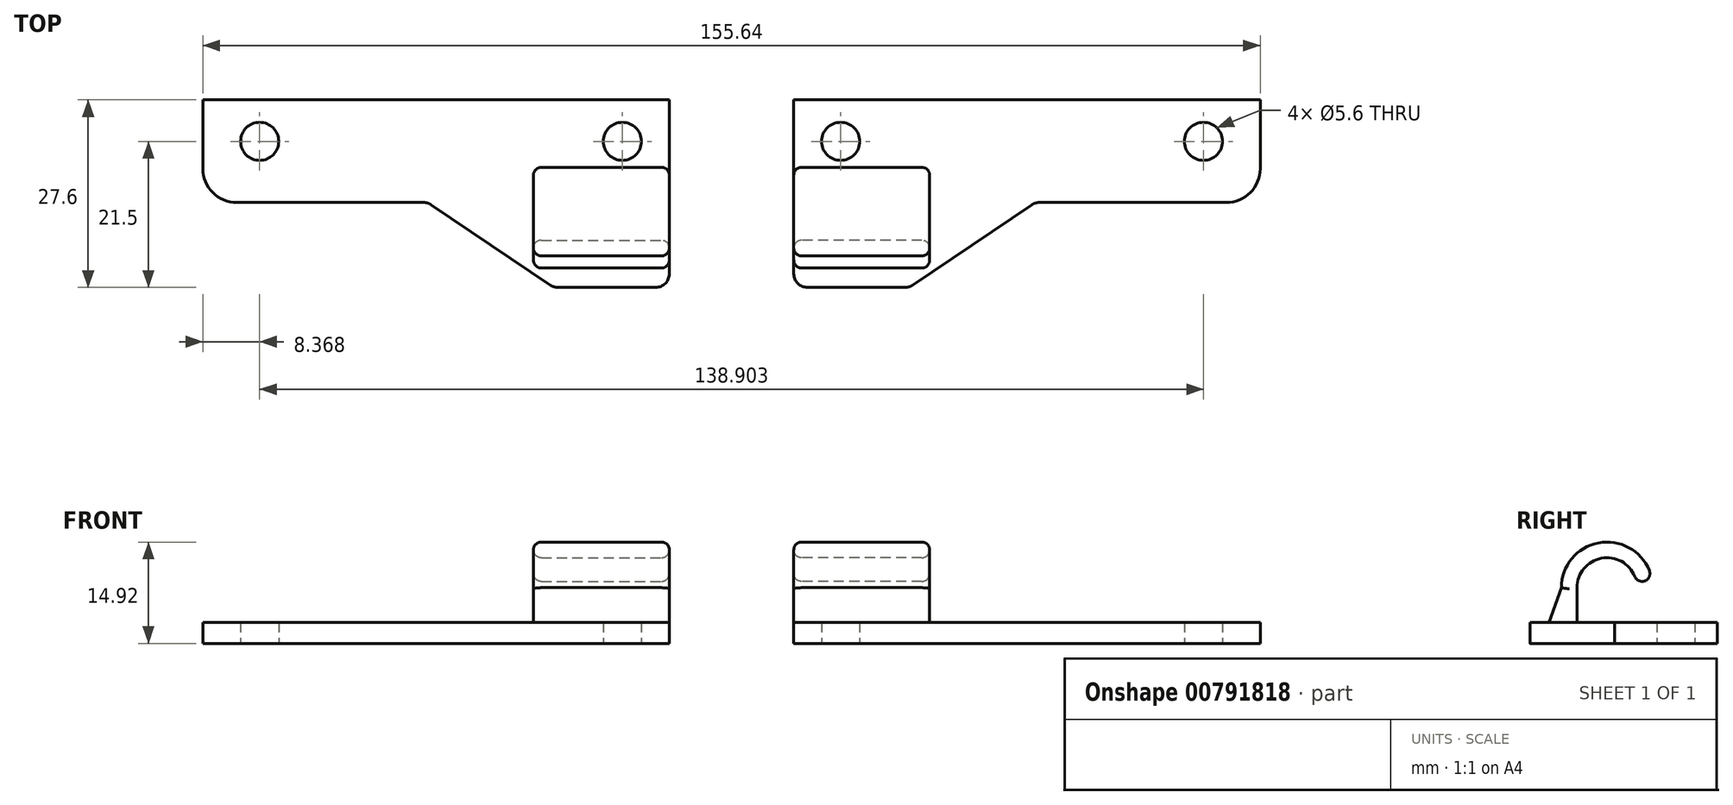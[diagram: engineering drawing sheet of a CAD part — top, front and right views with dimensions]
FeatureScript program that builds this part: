
annotation { "Feature Type Name" : "Feature", "Feature Type Description" : "" }
export const myFeature = defineFeature(function(context is Context, id is Id, definition is map)
    precondition{}
    {
        {
            var Q0;
            Q0=qCreatedBy(makeId("Top.planeOp"),FACE);
            var sketch = newSketch(context, id + "F0", { "sketchPlane" : qUnion([Q0])});
            skCircle(sketch, "E0", {"center": v(-17.35, 21.4) * mm, "radius": 2.8 * mm});
            skLineSegment(sketch, "E1", {"start": v(36.74, 27.5) * mm, "end": v(36.74, 21.3) * mm});
            skCircle(sketch, "E2", {"center": v(36.04, 21.4) * mm, "radius": 2.8 * mm});
            skPoint(sketch, "E3.visualSharp", {"position": v(-25.72, 27.5) * mm});
            skPoint(sketch, "E4.visualSharp", {"position": v(42.94, 27.5) * mm});
            skLineSegment(sketch, "E5", {"start": v(-25.72, 22.5) * mm, "end": v(-25.72, 17.4) * mm});
            skLineSegment(sketch, "E6", {"start": v(42.94, 12.4) * mm, "end": v(42.94, 22.5) * mm});
            skLineSegment(sketch, "E7", {"start": v(-25.72, 27.5) * mm, "end": v(-25.72, 22.5) * mm});
            skLineSegment(sketch, "E8", {"start": v(-20.72, 27.5) * mm, "end": v(-25.72, 27.5) * mm});
            skPoint(sketch, "E9.visualSharp", {"position": v(-25.72, 12.4) * mm});
            skArc(sketch, "E9.filletArc", {"start": v(-25.72, 17.4) * mm, "mid": v(-24.26, 13.86) * mm, "end": v(-20.72, 12.4) * mm});
            skLineSegment(sketch, "E10", {"start": v(37.94, 27.5) * mm, "end": v(42.94, 27.5) * mm});
            skLineSegment(sketch, "E11", {"start": v(42.94, 22.5) * mm, "end": v(42.94, 27.5) * mm});
            skLineSegment(sketch, "E12", {"start": v(42.94, 12.4) * mm, "end": v(42.94, 1.9) * mm});
            skLineSegment(sketch, "E13", {"start": v(26.55, -0.1) * mm, "end": v(40.94, -0.1) * mm});
            skLineSegment(sketch, "E14", {"start": v(25.43, 0.24) * mm, "end": v(7.9, 12.06) * mm});
            skPoint(sketch, "E15.visualSharp", {"position": v(42.94, -0.1) * mm});
            skArc(sketch, "E15.filletArc", {"start": v(40.94, -0.1) * mm, "mid": v(42.35, 0.49) * mm, "end": v(42.94, 1.9) * mm});
            skPoint(sketch, "E16.visualSharp", {"position": v(25.94, -0.1) * mm});
            skArc(sketch, "E16.filletArc", {"start": v(25.43, 0.24) * mm, "mid": v(25.97, -0.01) * mm, "end": v(26.55, -0.1) * mm});
            skPoint(sketch, "E17.visualSharp", {"position": v(7.4, 12.4) * mm});
            skArc(sketch, "E17.filletArc", {"start": v(7.9, 12.06) * mm, "mid": v(7.36, 12.31) * mm, "end": v(6.78, 12.4) * mm});
            skLineSegment(sketch, "E18", {"start": v(6.78, 12.4) * mm, "end": v(-20.72, 12.4) * mm});
            skLineSegment(sketch, "E19", {"start": v(-20.72, 27.5) * mm, "end": v(37.94, 27.5) * mm});
            skSolve(sketch);
        }
        {
            var Q0;
            Q0=qSketchRegion(id+"F0",true);
            extrude(context, id + "F1", {"entities" : qUnion([Q0]), "depth" : 3.1 * mm, "offsetDistance" : 25 * mm});
        }
        {
            var Q0;
            Q0=makeQuery(id+"F1.opExtrude","CAP_FACE",FACE,{"disambiguationData":[OSD([sQuery(id+"F0.wireOp",EDGE,"fae1df17-a2d7-4f6f-ac98-689a16ca2aa0.bottom"),sQuery(id+"F0.wireOp",EDGE,"E0"),sQuery(id+"F0.wireOp",EDGE,"E2"),sQuery(id+"F0.wireOp",EDGE,"E5"),sQuery(id+"F0.wireOp",EDGE,"E6"),sQuery(id+"F0.wireOp",EDGE,"E7"),sQuery(id+"F0.wireOp",EDGE,"E8"),sQuery(id+"F0.wireOp",EDGE,"E9.filletArc"),sQuery(id+"F0.wireOp",EDGE,"E10"),sQuery(id+"F0.wireOp",EDGE,"E11"),sQuery(id+"F0.wireOp",EDGE,"E12"),sQuery(id+"F0.wireOp",EDGE,"E13"),sQuery(id+"F0.wireOp",EDGE,"E14"),sQuery(id+"F0.wireOp",EDGE,"A2VAHK38-QV2u-fNEz-uaTx-NxCy4vqKou6f"),sQuery(id+"F0.wireOp",EDGE,"E15.filletArc"),sQuery(id+"F0.wireOp",EDGE,"E16.filletArc"),sQuery(id+"F0.wireOp",EDGE,"E17.filletArc")])],"isStart":false});
            var sketch = newSketch(context, id + "F2", { "sketchPlane" : qUnion([Q0])});
            skLineSegment(sketch, "E20.bottom", {"start": v(22.94, 6.84) * mm, "end": v(42.94, 6.84) * mm});
            skLineSegment(sketch, "E20.top", {"start": v(22.94, 4.54) * mm, "end": v(42.94, 4.54) * mm});
            skLineSegment(sketch, "E20.left", {"start": v(22.94, 6.84) * mm, "end": v(22.94, 4.54) * mm});
            skLineSegment(sketch, "E20.right", {"start": v(42.94, 6.84) * mm, "end": v(42.94, 4.54) * mm});
            skSolve(sketch);
        }
        {
            var Q0;
            Q0=qSketchRegion(id+"F2",true);
            extrude(context, id + "F3", {"entities" : qUnion([Q0]), "operationType" : NewBodyOperationType.ADD, "depth" : 5.1 * mm, "offsetDistance" : 25 * mm});
        }
        {
            var Q0;
            Q0=makeQuery(id+"F3.opExtrude","CAP_FACE",FACE,{"disambiguationData":[OSD([sQuery(id+"F2.wireOp",EDGE,"E20.bottom"),sQuery(id+"F2.wireOp",EDGE,"E20.top"),sQuery(id+"F2.wireOp",EDGE,"E20.left"),sQuery(id+"F2.wireOp",EDGE,"E20.right")])],"isStart":false});
            var sketch = newSketch(context, id + "F4", { "sketchPlane" : qUnion([Q0])});
            skLineSegment(sketch, "E21", {"start": v(22.94, 11.25) * mm, "end": v(42.94, 11.25) * mm});
            skSolve(sketch);
        }
        {
            var Q0;
            Q0=makeQuery(id+"F3.opExtrude","CAP_FACE",FACE,{"disambiguationData":[OSD([sQuery(id+"F2.wireOp",EDGE,"E20.bottom"),sQuery(id+"F2.wireOp",EDGE,"E20.top"),sQuery(id+"F2.wireOp",EDGE,"E20.left"),sQuery(id+"F2.wireOp",EDGE,"E20.right")])],"isStart":false});
            var Q1;
            Q1=sQuery(id+"F4.wireOp",EDGE,"E21");
            revolve(context, id + "F5", {"operationType" : NewBodyOperationType.ADD, "surfaceOperationType" : NewSurfaceOperationType.NEW, "entities" : qUnion([Q0]), "axis" : qUnion([Q1]), "revolveType" : RevolveType.ONE_DIRECTION, "oppositeDirection" : true, "angle" : 170 * degree});
        }
        {
            var Q0;
            Q0=makeQuery(id+"F5.opRevolve","CAP_EDGE",EDGE,{"disambiguationData":[OSD([sQuery(id+"F2.wireOp",EDGE,"E20.bottom")])],"isStart":false});
            var Q1;
            Q1=makeQuery(id+"F5.opRevolve","CAP_EDGE",EDGE,{"disambiguationData":[OSD([sQuery(id+"F2.wireOp",EDGE,"E20.top")])],"isStart":false});
            fillet(context, id + "F6", {"entities" : qUnion([Q0, Q1]), "radius" : 1.15 * mm, "tangentPropagation" : true, "allowEdgeOverflow" : false});
        }
        {
            var Q0;
            {var subQ0=sQuery(id+"F2.wireOp",EDGE,"E20.left");Q0=makeQuery(id+"F5.boolean.opBoolean","MERGE",FACE,{"derivedFrom":[makeQuery(id+"F3.opExtrude","SWEPT_FACE",FACE,{"disambiguationData":[OSD([subQ0])]}),makeQuery(id+"F5.opRevolve","SWEPT_FACE",FACE,{"disambiguationData":[OSD([subQ0])]})]});}
            var sketch = newSketch(context, id + "F7", { "sketchPlane" : qUnion([Q0])});
            skLineSegment(sketch, "E22", {"start": v(-4.54, 8.2) * mm, "end": v(-2.74, 3.1) * mm});
            skLineSegment(sketch, "E23", {"start": v(-2.74, 3.1) * mm, "end": v(-4.54, 3.1) * mm});
            skLineSegment(sketch, "E24", {"start": v(-4.54, 8.2) * mm, "end": v(-4.54, 3.1) * mm});
            skSolve(sketch);
        }
        {
            var Q0;
            Q0=qSketchRegion(id+"F7",true);
            extrude(context, id + "F8", {"entities" : qUnion([Q0]), "operationType" : NewBodyOperationType.ADD, "oppositeDirection" : true, "depth" : 20 * mm, "offsetDistance" : 25 * mm});
        }
        {
            var Q0;
            Q0=makeQuery(id+"F8.opExtrude","CAP_EDGE",EDGE,{"disambiguationData":[OSD([sQuery(id+"F7.wireOp",EDGE,"E22")])],"isStart":true});
            var Q1;
            Q1=makeQuery(id+"F5.opRevolve","SWEPT_EDGE",EDGE,{"disambiguationData":[OSD([sQuery(id+"F2.wireOp",EDGE,"E20.top"),sQuery(id+"F2.wireOp",EDGE,"E20.left")])]});
            var Q2;
            Q2=makeQuery(id+"F8.opExtrude","CAP_EDGE",EDGE,{"disambiguationData":[OSD([sQuery(id+"F7.wireOp",EDGE,"E22")])],"isStart":false});
            var Q3;
            Q3=makeQuery(id+"F5.opRevolve","SWEPT_EDGE",EDGE,{"disambiguationData":[OSD([sQuery(id+"F2.wireOp",EDGE,"E20.top"),sQuery(id+"F2.wireOp",EDGE,"E20.right")])]});
            fillet(context, id + "F9", {"entities" : qUnion([Q0, Q1, Q2, Q3]), "radius" : 1.14 * mm, "tangentPropagation" : true, "allowEdgeOverflow" : false});
        }
        {
            var Q0;
            Q0=makeQuery(id+"F1.opExtrude","SWEPT_BODY",BODY,{"disambiguationData":[OSD([sQuery(id+"F0.wireOp",EDGE,"fae1df17-a2d7-4f6f-ac98-689a16ca2aa0.bottom"),sQuery(id+"F0.wireOp",EDGE,"E0"),sQuery(id+"F0.wireOp",EDGE,"E2"),sQuery(id+"F0.wireOp",EDGE,"E5"),sQuery(id+"F0.wireOp",EDGE,"E6"),sQuery(id+"F0.wireOp",EDGE,"E7"),sQuery(id+"F0.wireOp",EDGE,"E8"),sQuery(id+"F0.wireOp",EDGE,"E9.filletArc"),sQuery(id+"F0.wireOp",EDGE,"E10"),sQuery(id+"F0.wireOp",EDGE,"E11"),sQuery(id+"F0.wireOp",EDGE,"E12"),sQuery(id+"F0.wireOp",EDGE,"E13"),sQuery(id+"F0.wireOp",EDGE,"E14"),sQuery(id+"F0.wireOp",EDGE,"A2VAHK38-QV2u-fNEz-uaTx-NxCy4vqKou6f"),sQuery(id+"F0.wireOp",EDGE,"E15.filletArc"),sQuery(id+"F0.wireOp",EDGE,"E16.filletArc"),sQuery(id+"F0.wireOp",EDGE,"E17.filletArc")])]});
            transform(context, id + "F10", {"entities" : qUnion([Q0]), "transformType" : TransformType.TRANSLATION_3D, "dx" : -52.1 * mm, "dy" : 0 * mm, "dz" : 0 * mm, "makeCopy" : false});
        }
        {
            var Q0;
            Q0=makeQuery(id+"F1.opExtrude","SWEPT_BODY",BODY,{"disambiguationData":[OSD([sQuery(id+"F0.wireOp",EDGE,"fae1df17-a2d7-4f6f-ac98-689a16ca2aa0.bottom"),sQuery(id+"F0.wireOp",EDGE,"E0"),sQuery(id+"F0.wireOp",EDGE,"E2"),sQuery(id+"F0.wireOp",EDGE,"E5"),sQuery(id+"F0.wireOp",EDGE,"E6"),sQuery(id+"F0.wireOp",EDGE,"E7"),sQuery(id+"F0.wireOp",EDGE,"E8"),sQuery(id+"F0.wireOp",EDGE,"E9.filletArc"),sQuery(id+"F0.wireOp",EDGE,"E10"),sQuery(id+"F0.wireOp",EDGE,"E11"),sQuery(id+"F0.wireOp",EDGE,"E12"),sQuery(id+"F0.wireOp",EDGE,"E13"),sQuery(id+"F0.wireOp",EDGE,"E14"),sQuery(id+"F0.wireOp",EDGE,"A2VAHK38-QV2u-fNEz-uaTx-NxCy4vqKou6f"),sQuery(id+"F0.wireOp",EDGE,"E15.filletArc"),sQuery(id+"F0.wireOp",EDGE,"E16.filletArc"),sQuery(id+"F0.wireOp",EDGE,"E17.filletArc")])]});
            var Q1;
            Q1=qCreatedBy(makeId("Right.planeOp"),FACE);
            mirror(context, id + "F11", {"entities" : qUnion([Q0]), "mirrorPlane" : qUnion([Q1])});
        }
    });
